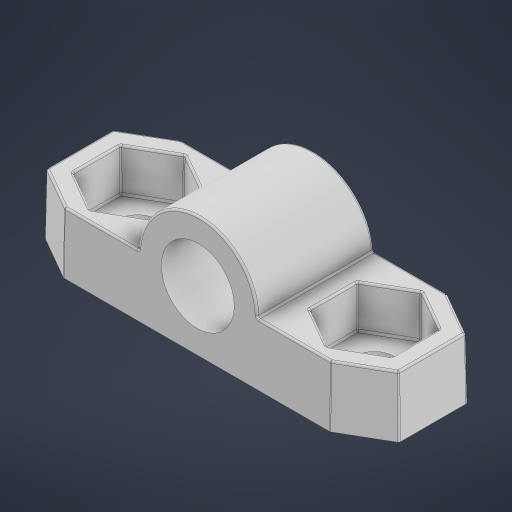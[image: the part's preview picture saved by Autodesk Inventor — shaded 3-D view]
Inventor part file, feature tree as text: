
AUTODESK INVENTOR PART (.ipt)
format: ipt  version: 2023 (Build 270158000, 158)  size: 768,512 bytes
history: native  units: in
note: dims shown in document units (in); Inventor stores cm internally (conversion verified against a paired STEP export)
features: fillet x1
ambient origin geometry x8: Origin, YZ Plane, XZ Plane, XY Plane, X Axis, Y Axis, Z Axis, Center Point
bodies: Solid1 (feature_tree)
feature tree (1):
  fillet  "Fillet7"  [1 undecoded]
note: 1 required parameter value undecoded (feature->parameter linkage not recoverable at this tier; creation-order binding heuristic only, values carry confidence <= 0.55)
